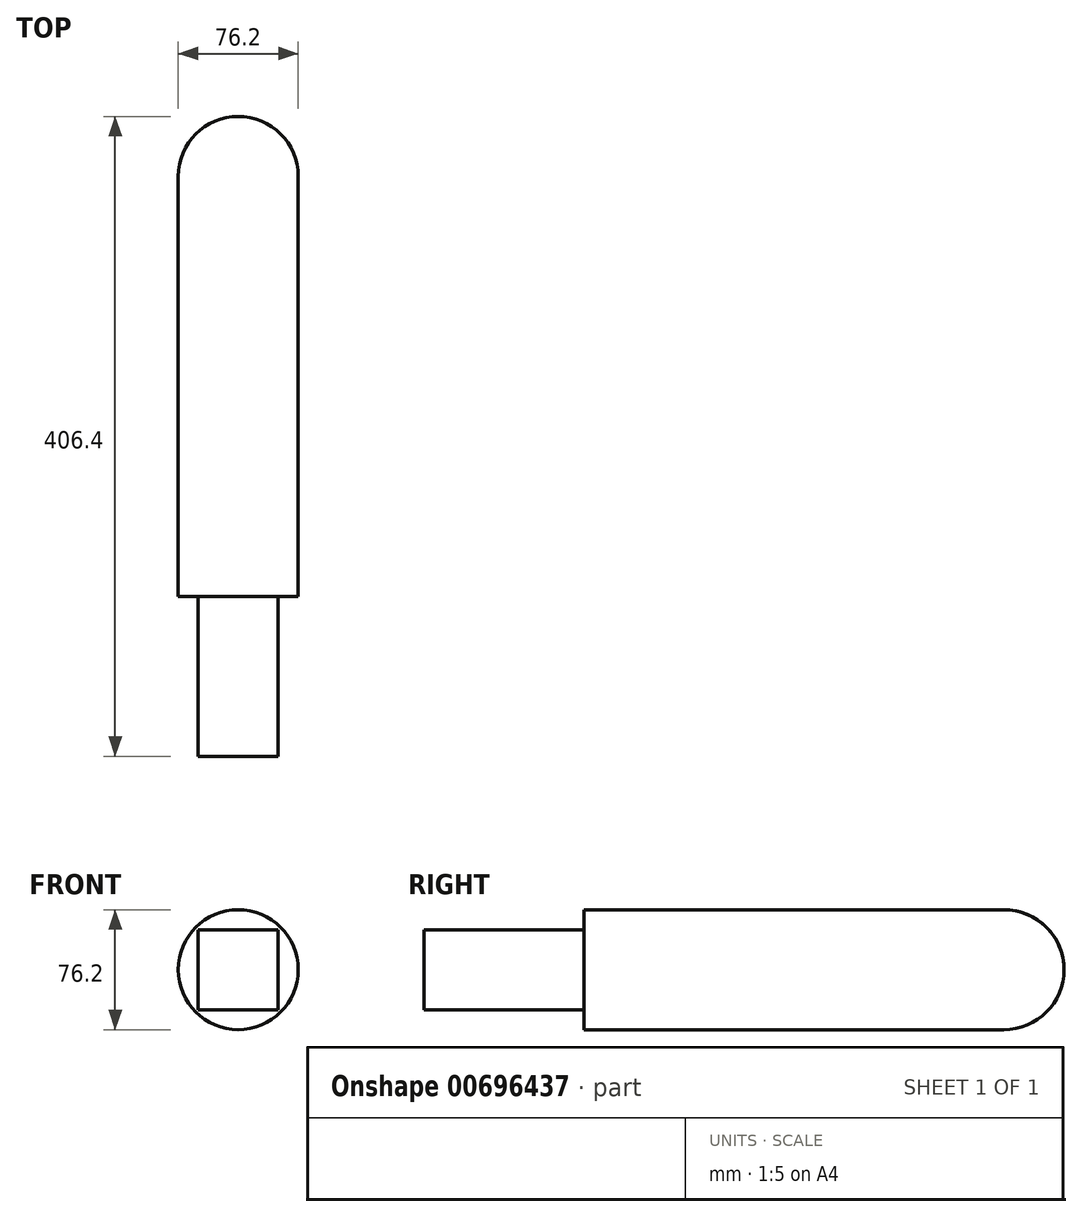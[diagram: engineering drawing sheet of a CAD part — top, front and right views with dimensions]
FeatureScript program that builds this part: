
annotation { "Feature Type Name" : "Feature", "Feature Type Description" : "" }
export const myFeature = defineFeature(function(context is Context, id is Id, definition is map)
    precondition{}
    {
        {
            var Q0;
            Q0=qCreatedBy(makeId("Front.planeOp"),FACE);
            var sketch = newSketch(context, id + "F0", { "sketchPlane" : qUnion([Q0])});
            skLineSegment(sketch, "E0.bottom", {"start": v(25.4, 25.4) * mm, "end": v(-25.4, 25.4) * mm});
            skLineSegment(sketch, "E0.top", {"start": v(25.4, -25.4) * mm, "end": v(-25.4, -25.4) * mm});
            skLineSegment(sketch, "E0.left", {"start": v(25.4, 25.4) * mm, "end": v(25.4, -25.4) * mm});
            skLineSegment(sketch, "E0.right", {"start": v(-25.4, 25.4) * mm, "end": v(-25.4, -25.4) * mm});
            skPoint(sketch, "E0.middle", {"position": v(0, 0) * mm});
            skSolve(sketch);
        }
        {
            var Q0;
            Q0 = qSketchRegion(id + "F0", true);
            extrude(context, id + "F1", {"entities" : qUnion([Q0]), "depth" : 101.6 * mm, "offsetDistance" : 25.4 * mm});
        }
        {
            var Q0;
            Q0=makeQuery(id+"F1.opExtrude","CAP_FACE",FACE,{"disambiguationData":[OSD([sQuery(id+"F0.wireOp",EDGE,"E0.bottom"),sQuery(id+"F0.wireOp",EDGE,"E0.top"),sQuery(id+"F0.wireOp",EDGE,"E0.left"),sQuery(id+"F0.wireOp",EDGE,"E0.right")])],"isStart":true});
            var sketch = newSketch(context, id + "F2", { "sketchPlane" : qUnion([Q0])});
            skCircle(sketch, "E1", {"center": v(0, 0) * mm, "radius": 38.1 * mm});
            skSolve(sketch);
        }
        {
            var Q0;
            Q0 = qSketchRegion(id + "F2", true);
            extrude(context, id + "F3", {"entities" : qUnion([Q0]), "operationType" : NewBodyOperationType.ADD, "depth" : 304.8 * mm, "offsetDistance" : 25.4 * mm});
        }
        {
            var Q0;
            Q0=makeQuery(id+"F3.opExtrude","CAP_EDGE",EDGE,{"disambiguationData":[OSD([sQuery(id+"F2.wireOp",EDGE,"E1")])],"isStart":false});
            fillet(context, id + "F4", {"entities" : qUnion([Q0]), "radius" : 38.1 * mm, "tangentPropagation" : true, "allowEdgeOverflow" : false});
        }
    });
